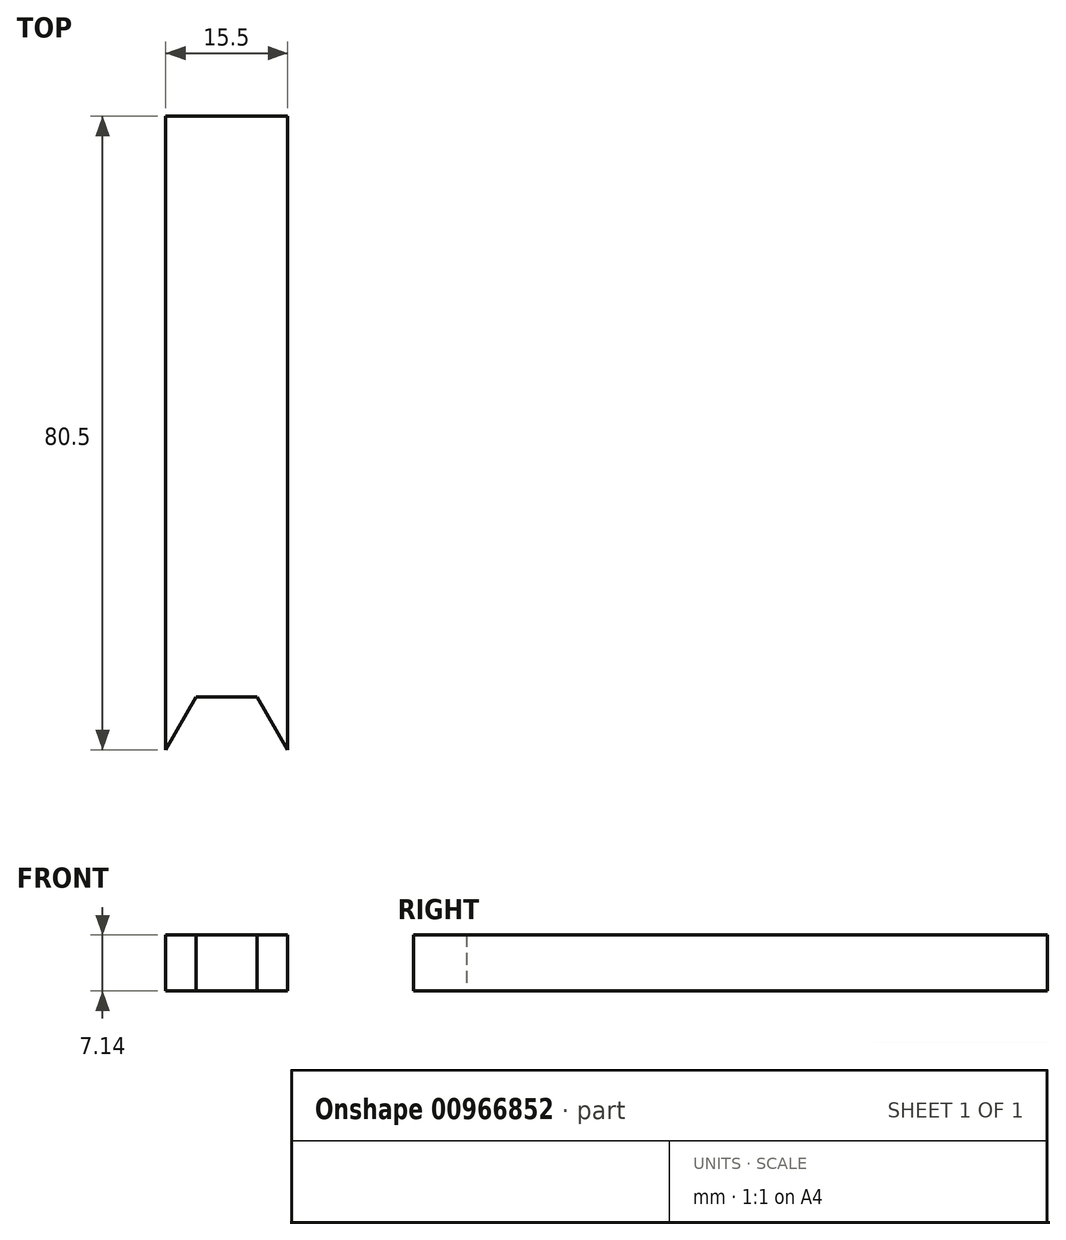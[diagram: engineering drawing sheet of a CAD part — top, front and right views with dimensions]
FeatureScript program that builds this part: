
annotation { "Feature Type Name" : "Feature", "Feature Type Description" : "" }
export const myFeature = defineFeature(function(context is Context, id is Id, definition is map)
    precondition{}
    {
        {
            var Q0;
            Q0=qCreatedBy(makeId("Top.planeOp"),FACE);
            var sketch = newSketch(context, id + "F0", { "sketchPlane" : qUnion([Q0])});
            skLineSegment(sketch, "E0.bottom", {"start": v(7.75, 40.25) * mm, "end": v(-7.75, 40.25) * mm});
            skLineSegment(sketch, "E0.top", {"start": v(7.75, -40.25) * mm, "end": v(-7.75, -40.25) * mm});
            skLineSegment(sketch, "E0.left", {"start": v(7.75, 40.25) * mm, "end": v(7.75, -40.25) * mm});
            skLineSegment(sketch, "E0.right", {"start": v(-7.75, 40.25) * mm, "end": v(-7.75, -40.25) * mm});
            skPoint(sketch, "E0.middle", {"position": v(0, 0) * mm});
            skCircle(sketch, "E1.cCircle", {"center": v(0, -40.25) * mm, "radius": 6.7 * mm, "construction": true});
            skLineSegment(sketch, "E1.0", {"start": v(-3.87, -33.54) * mm, "end": v(3.87, -33.54) * mm});
            skLineSegment(sketch, "E1.1", {"start": v(3.87, -33.54) * mm, "end": v(7.75, -40.25) * mm});
            skLineSegment(sketch, "E1.2", {"start": v(7.75, -40.25) * mm, "end": v(3.87, -46.96) * mm});
            skLineSegment(sketch, "E1.3", {"start": v(3.87, -46.96) * mm, "end": v(-3.87, -46.96) * mm});
            skLineSegment(sketch, "E1.4", {"start": v(-3.87, -46.96) * mm, "end": v(-7.75, -40.25) * mm});
            skLineSegment(sketch, "E1.5", {"start": v(-7.75, -40.25) * mm, "end": v(-3.87, -33.54) * mm});
            skPoint(sketch, "E1.0.midPoint", {"position": v(0, -33.54) * mm});
            skSolve(sketch);
        }
        {
            var Q0;
            Q0=makeQuery(id+"F0.imprint","IMPRINT",FACE,{"disambiguationData":[TD([[makeQuery(id+"F0.imprint","IMPRINT",EDGE,{"derivedFrom":sQuery(id+"F0.wireOp",EDGE,"E0.bottom")}),1.0]])]});
            extrude(context, id + "F1", {"entities" : qUnion([Q0]), "depth" : 7.14 * mm, "offsetDistance" : 25.4 * mm});
        }
    });
